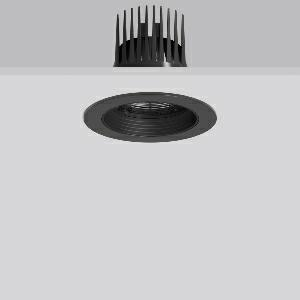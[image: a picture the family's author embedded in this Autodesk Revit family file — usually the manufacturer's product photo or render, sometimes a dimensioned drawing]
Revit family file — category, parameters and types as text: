
# Revit family: heledon_maxi_e_901761_003_3_76_9dbd
name_source: partatom
category: Lighting Fixtures
units: mm (PartAtom-declared; Revit-internal decimal feet)

## family parameters
Cut with Voids When Loaded = No
Host = Face
Light Source = No
Part Type = Normal
Room Calculation Point = No
Round Connector Dimension = Use Diameter
Shared = No

## types (1)
- HELEDON maxi E (1 x LED Modul 935, 2800 lm, 3500)
    Apparent Load = 25 VA
    Approval mark = CE
    CIE Flux Codes = 96 100 100 100 100
    Color Rendering = 92
    Color Temperature = 3500
    Default Elevation = 1800 mm
    Description = Series: HELEDON maxi
Round recessed downlight. Housing: die-cast aluminium, powder-coated. Black plastic ring and recessed LED to prevent glare from the side. Optical assembly with lens made of plastic (polycarbonate) for the best homogeneous light distribution - can be changed without tools. Best colour rendering index Ra>90. Suitable for Recessed ceiling mounting. Installation without tools thanks to spring fastening system. Including separate LED converter with connecting cable 600 mm.High quality converter without flickering and stroboscopic effect. Through-wiring box (5 pole) available as accessory. The following accessories can be mounted without use of tools: interchangeable lenses, decorative glasses, honeycomb louvre, clear and frosted diffusers, white interchangeable plastic ring. 
Colour: deep black, matt (RAL 9005)
Diameter: 162 mm
Height: 3 mm
Cut-out diameter: 152 mm
Recess height: 200 mm
Luminaire: recess height: 135 mm
Lamp: LED
Socket: without socket
Colour temperature: 3500K
Colour rendering index (CRI): 92
System power: 25 W
Rated luminous flux: 2800 lm
Luminous efficiency: 112 lm/W
Control gear: Converter, dimmable, DALI
Protection class: II
Type of protection: IP 20
    Height = 0 mm  [stored 0 ft]
    Lamp = 1 x LED Modul 935
    Lamp Light Flux = 2800 lm
    Lamp count = 1
    Length = 162 mm
    Lifetime = 50000 h
    Luminous efficacy = 112 lm/W
    Manufacturer = RZB
    ModVariant = No
    Model = 901761.003.3.76
    Mounting Place = Ceiling
    Mounting Type = Recessed
    Number of Poles = 1
    OnlyDefault = Yes
    Power Factor = 1
    Product Name = HELEDON maxi E
    Product group = Recessed downlights
    ProductGroupID = 402
    Protection Class = Protection class II
    Protection Degree = IP 20
    RLX_Detail_Level = 1
    RLX_Emergency_Light_Flux = 0 lm
    RLX_Emergency_Type = 0
    RLX_Emergency_Type_DB = No
    RlxData = <blob elided: 123777 chars, md5=066aba40>
    Socket = socket
    Standby Power = 0 W
    System Light Flux = 2800 lm
    System Power = 25 W
    Type Comments = Product without accessories
    Type Image = 901663.003.jpg
    URL = http://relux.com
    VarID = ---
    Voltage = 230 V
    Voltage Range = 220-240 V
    Weight = 0.00 kg
    Width = 0 mm  [stored 0 ft]

note: [stored X ft] marks values corroborated as IEEE doubles in the binary element streams (Revit-internal decimal feet)

## geometry (parser evidence)
native form markers: Blend x4, Sweep x11
no freeform markers — native parametric forms only
